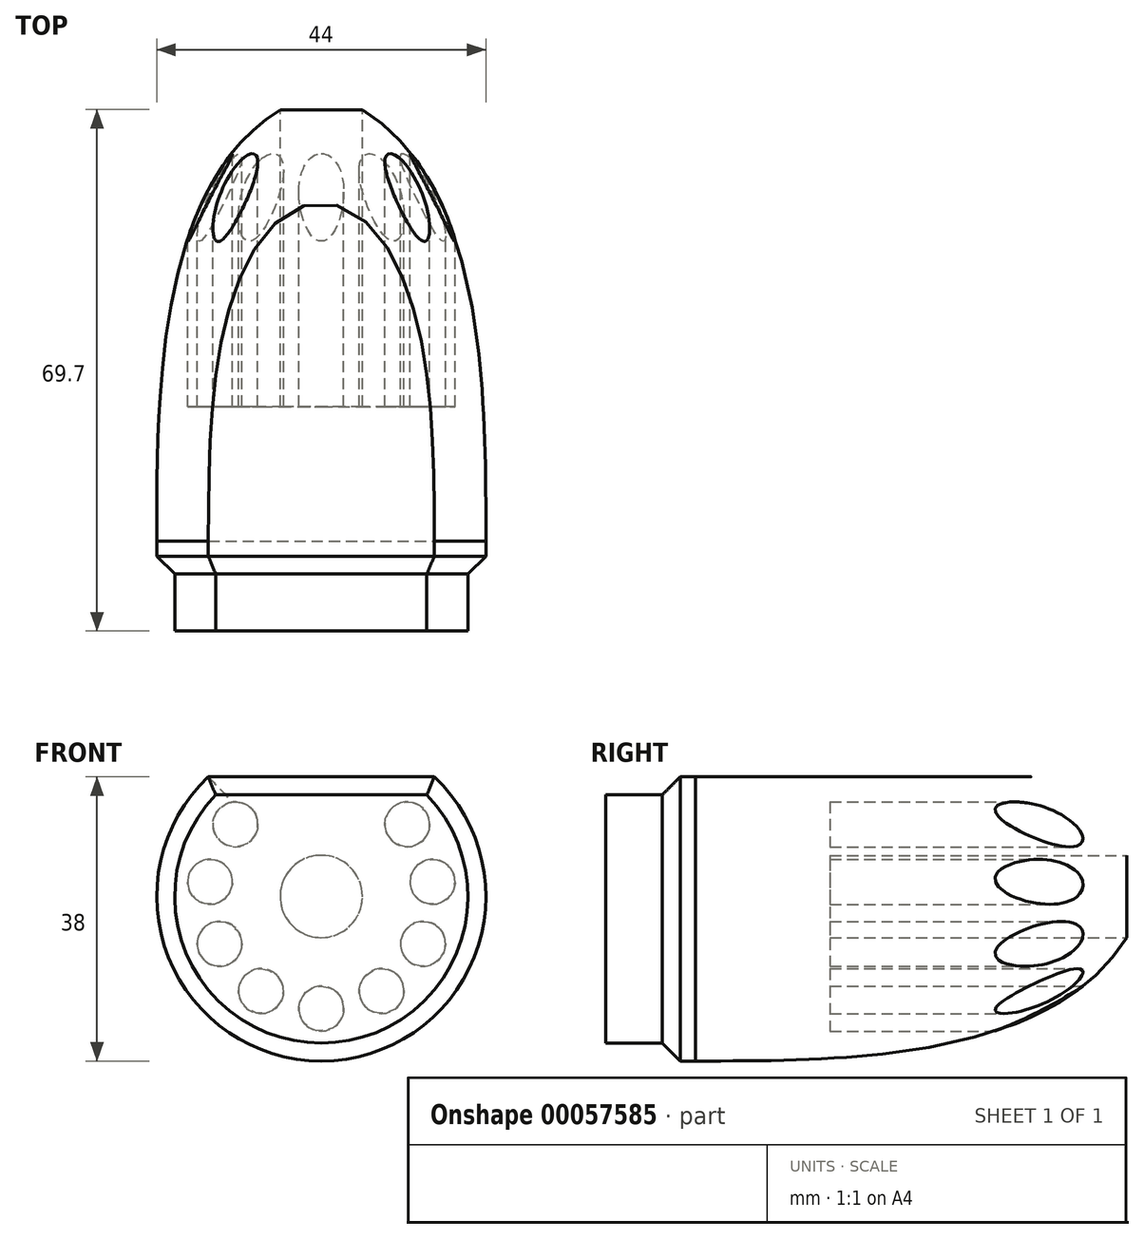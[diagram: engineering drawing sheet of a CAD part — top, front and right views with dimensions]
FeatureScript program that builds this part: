
annotation { "Feature Type Name" : "Feature", "Feature Type Description" : "" }
export const myFeature = defineFeature(function(context is Context, id is Id, definition is map)
    precondition{}
    {
        {
            var Q0;
            Q0=qCreatedBy(makeId("Right.planeOp"),FACE);
            var sketch = newSketch(context, id + "F0", { "sketchPlane" : qUnion([Q0])});
            skLineSegment(sketch, "E0", {"start": v(0, 0) * mm, "end": v(0, 22) * mm});
            skLineSegment(sketch, "E1", {"start": v(0, 0) * mm, "end": v(70, 0) * mm});
            skLineSegment(sketch, "E2", {"start": v(0, 22) * mm, "end": v(12, 22) * mm});
            skLineSegment(sketch, "E3", {"start": v(70, 0) * mm, "end": v(70, 5) * mm});
            skFitSpline(sketch, "E4", {"points": [v(12, 22) * mm, v(70, 5) * mm], "startDerivative": vector(60, 0) * mm, "endDerivative": vector(30, -51) * mm});
            skSolve(sketch);
        }
        {
            var Q0;
            Q0 = qSketchRegion(id + "F0", true);
            var Q1;
            Q1=sQuery(id+"F0.wireOp",EDGE,"E1");
            revolve(context, id + "F1", {"entities" : qUnion([Q0]), "axis" : qUnion([Q1]), "revolveType" : RevolveType.FULL});
        }
        {
            var Q0;
            Q0=qCreatedBy(makeId("Right.planeOp"),FACE);
            var sketch = newSketch(context, id + "F2", { "sketchPlane" : qUnion([Q0])});
            skLineSegment(sketch, "E5.bottom", {"start": v(0, 22) * mm, "end": v(60, 22) * mm});
            skLineSegment(sketch, "E5.top", {"start": v(0, 16) * mm, "end": v(60, 16) * mm});
            skLineSegment(sketch, "E5.left", {"start": v(0, 22) * mm, "end": v(0, 16) * mm});
            skLineSegment(sketch, "E5.right", {"start": v(60, 22) * mm, "end": v(60, 16) * mm});
            skSolve(sketch);
        }
        {
            var Q0;
            Q0 = qSketchRegion(id + "F2", true);
            extrude(context, id + "F3", {"entities" : qUnion([Q0]), "operationType" : NewBodyOperationType.REMOVE, "endBound" : BoundingType.SYMMETRIC, "oppositeDirection" : true, "depth" : 44 * mm});
        }
        {
            var Q0;
            Q0=makeQuery(id+"F1.opRevolve","SWEPT_FACE",FACE,{"disambiguationData":[OSD([sQuery(id+"F0.wireOp",EDGE,"E0")])]});
            var sketch = newSketch(context, id + "F4", { "sketchPlane" : qUnion([Q0])});
            skLineSegment(sketch, "E6.0", {"start": v(-15.1, 16) * mm, "end": v(15.1, 16) * mm});
            skArc(sketch, "E6.1", {"start": v(-15.1, 16) * mm, "mid": v(0, -22) * mm, "end": v(15.1, 16) * mm});
            skLineSegment(sketch, "E7.0", {"start": v(-14.11, 13.6) * mm, "end": v(14.11, 13.6) * mm});
            skArc(sketch, "E7.1", {"start": v(-14.11, 13.6) * mm, "mid": v(0, -19.6) * mm, "end": v(14.11, 13.6) * mm});
            skSolve(sketch);
        }
        {
            var Q0;
            Q0 = qSketchRegion(id + "F4", true);
            extrude(context, id + "F5", {"entities" : qUnion([Q0]), "operationType" : NewBodyOperationType.REMOVE, "oppositeDirection" : true, "depth" : 10 * mm});
        }
        {
            var Q0;
            Q0=makeQuery(id+"F5.boolean.opBoolean","COPY",EDGE,{"derivedFrom":makeQuery(id+"F5.opExtrude","CAP_EDGE",EDGE,{"disambiguationData":[OSD([sQuery(id+"F4.wireOp",EDGE,"E7.1")])],"isStart":false})});
            var Q1;
            Q1=makeQuery(id+"F5.boolean.opBoolean","COPY",EDGE,{"derivedFrom":makeQuery(id+"F5.opExtrude","CAP_EDGE",EDGE,{"disambiguationData":[OSD([sQuery(id+"F4.wireOp",EDGE,"E7.0")])],"isStart":false})});
            chamfer(context, id + "F6", {"entities" : qUnion([Q0, Q1]), "width" : 2.4 * mm});
        }
        {
            var Q0;
            Q0=makeQuery(id+"F1.opRevolve","SWEPT_FACE",FACE,{"disambiguationData":[OSD([sQuery(id+"F0.wireOp",EDGE,"E3")])]});
            var sketch = newSketch(context, id + "F7", { "sketchPlane" : qUnion([Q0])});
            skCircle(sketch, "E8", {"center": v(0, 0) * mm, "radius": 15 * mm, "construction": true});
            skCircle(sketch, "E9", {"center": v(11.5, 9.64) * mm, "radius": 3 * mm});
            skLineSegment(sketch, "E10", {"start": v(0, 0) * mm, "end": v(11.5, 9.64) * mm, "construction": true});
            skCircle(sketch, "E11.1.0", {"center": v(14.87, 1.96) * mm, "radius": 3 * mm});
            skCircle(sketch, "E11.2.0", {"center": v(13.6, -6.34) * mm, "radius": 3 * mm});
            skCircle(sketch, "E11.3.0", {"center": v(8.06, -12.65) * mm, "radius": 3 * mm});
            skCircle(sketch, "E11.4.0", {"center": v(0, -15) * mm, "radius": 3 * mm});
            skCircle(sketch, "E11.5.0", {"center": v(-8.06, -12.65) * mm, "radius": 3 * mm});
            skCircle(sketch, "E11.6.0", {"center": v(-13.6, -6.34) * mm, "radius": 3 * mm});
            skCircle(sketch, "E11.7.0", {"center": v(-14.87, 1.96) * mm, "radius": 3 * mm});
            skCircle(sketch, "E11.8.0", {"center": v(-11.5, 9.64) * mm, "radius": 3 * mm});
            skLineSegment(sketch, "E11.anchor2", {"start": v(0, 0) * mm, "end": v(-11.5, 9.64) * mm, "construction": true});
            skCircle(sketch, "E12", {"center": v(0, 0) * mm, "radius": 5.5 * mm});
            skSolve(sketch);
        }
        {
            var Q0;
            Q0 = qSketchRegion(id + "F7", true);
            extrude(context, id + "F8", {"entities" : qUnion([Q0]), "operationType" : NewBodyOperationType.REMOVE, "oppositeDirection" : true, "depth" : 40 * mm});
        }
    });
